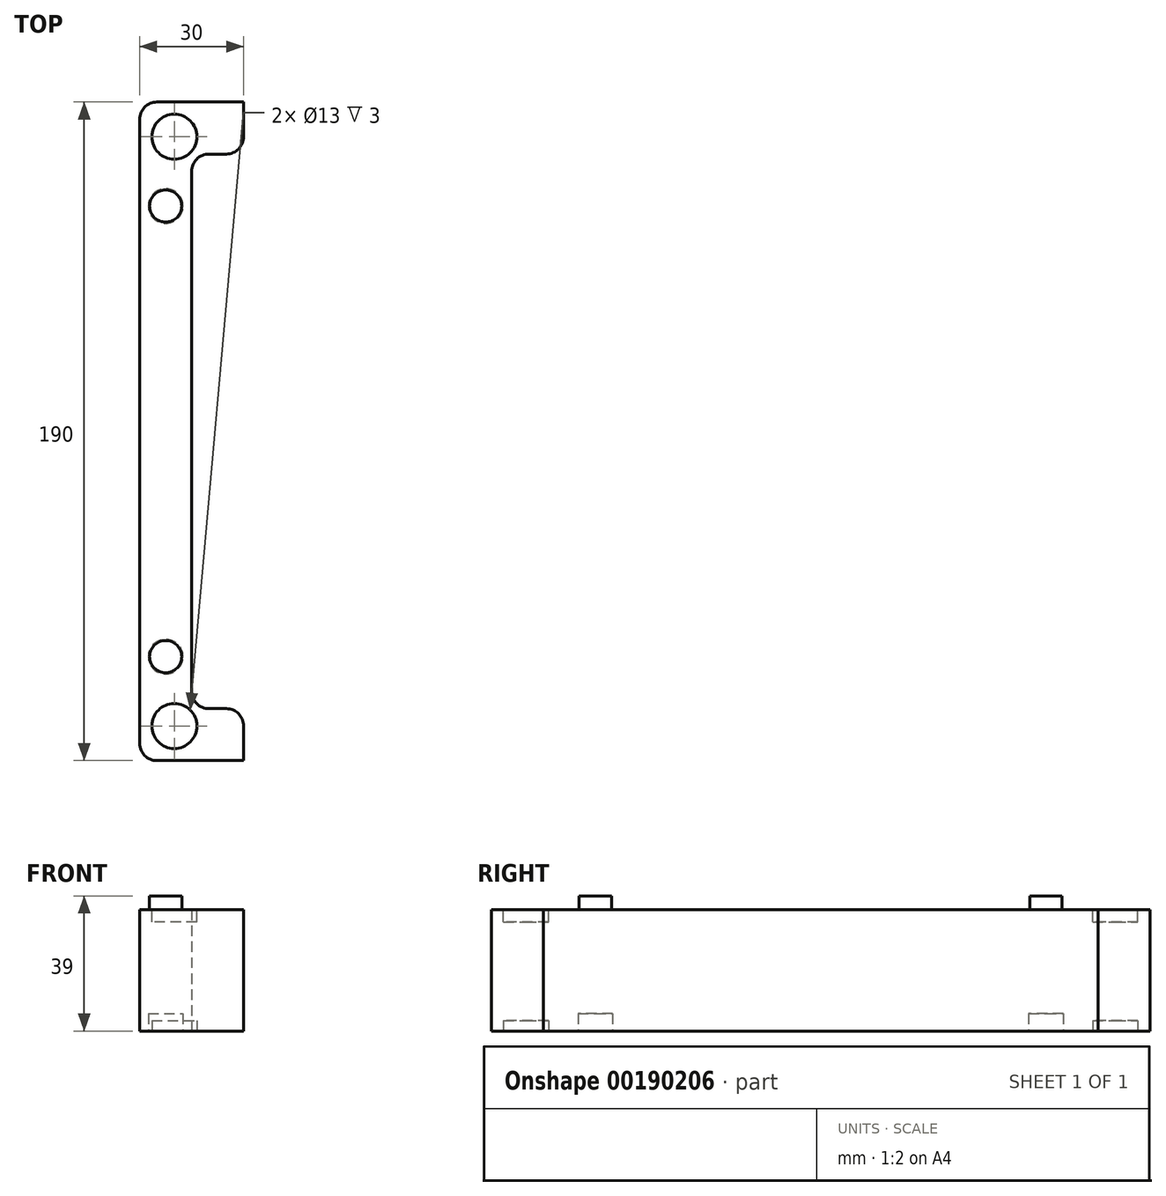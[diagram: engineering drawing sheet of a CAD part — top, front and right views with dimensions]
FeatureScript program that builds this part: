
annotation { "Feature Type Name" : "Feature", "Feature Type Description" : "" }
export const myFeature = defineFeature(function(context is Context, id is Id, definition is map)
    precondition{}
    {
        {
            var Q0;
            Q0=qCreatedBy(makeId("Top.planeOp"),FACE);
            var sketch = newSketch(context, id + "F0", { "sketchPlane" : qUnion([Q0])});
            skLineSegment(sketch, "E0.left", {"start": v(18.75, 91.13) * mm, "end": v(18.75, 81.13) * mm});
            skLineSegment(sketch, "E1", {"start": v(3.75, 71.13) * mm, "end": v(3.75, -78.87) * mm});
            skLineSegment(sketch, "E2", {"start": v(8.75, -83.87) * mm, "end": v(13.75, -83.87) * mm});
            skLineSegment(sketch, "E3", {"start": v(8.75, 76.13) * mm, "end": v(13.75, 76.13) * mm});
            skLineSegment(sketch, "E4.trimOffspring", {"start": v(18.75, -88.87) * mm, "end": v(18.75, -98.87) * mm});
            skLineSegment(sketch, "E5", {"start": v(18.75, 91.13) * mm, "end": v(-6.25, 91.13) * mm});
            skLineSegment(sketch, "E6", {"start": v(18.75, -98.87) * mm, "end": v(-6.25, -98.87) * mm});
            skLineSegment(sketch, "E7", {"start": v(-11.25, 86.13) * mm, "end": v(-11.25, -93.87) * mm});
            skPoint(sketch, "E8.visualSharp", {"position": v(-11.25, -98.87) * mm});
            skArc(sketch, "E8.filletArc", {"start": v(-11.25, -93.87) * mm, "mid": v(-9.79, -97.4) * mm, "end": v(-6.25, -98.87) * mm});
            skPoint(sketch, "E9.visualSharp", {"position": v(-11.25, 91.13) * mm});
            skArc(sketch, "E9.filletArc", {"start": v(-6.25, 91.13) * mm, "mid": v(-9.79, 89.66) * mm, "end": v(-11.25, 86.13) * mm});
            skPoint(sketch, "E10.visualSharp", {"position": v(18.75, 76.13) * mm});
            skArc(sketch, "E10.filletArc", {"start": v(13.75, 76.13) * mm, "mid": v(17.28, 77.6) * mm, "end": v(18.75, 81.13) * mm});
            skPoint(sketch, "E11.visualSharp", {"position": v(18.75, -83.87) * mm});
            skArc(sketch, "E11.filletArc", {"start": v(18.75, -88.87) * mm, "mid": v(17.28, -85.34) * mm, "end": v(13.75, -83.87) * mm});
            skPoint(sketch, "E12.visualSharp", {"position": v(3.75, -83.87) * mm});
            skArc(sketch, "E12.filletArc", {"start": v(3.75, -78.87) * mm, "mid": v(5.21, -82.4) * mm, "end": v(8.75, -83.87) * mm});
            skPoint(sketch, "E13.visualSharp", {"position": v(3.75, 76.13) * mm});
            skArc(sketch, "E13.filletArc", {"start": v(8.75, 76.13) * mm, "mid": v(5.21, 74.66) * mm, "end": v(3.75, 71.13) * mm});
            skSolve(sketch);
        }
        {
            var Q0;
            Q0 = qSketchRegion(id + "F0", true);
            extrude(context, id + "F1", {"entities" : qUnion([Q0]), "depth" : 35 * mm, "offsetDistance" : 25 * mm});
        }
        {
            var Q0;
            Q0=makeQuery(id+"F1.opExtrude","CAP_FACE",FACE,{"disambiguationData":[OSD([sQuery(id+"F0.wireOp",EDGE,"E0.left"),sQuery(id+"F0.wireOp",EDGE,"E1"),sQuery(id+"F0.wireOp",EDGE,"E2"),sQuery(id+"F0.wireOp",EDGE,"E3"),sQuery(id+"F0.wireOp",EDGE,"E4.trimOffspring"),sQuery(id+"F0.wireOp",EDGE,"E5"),sQuery(id+"F0.wireOp",EDGE,"E6"),sQuery(id+"F0.wireOp",EDGE,"E7"),sQuery(id+"F0.wireOp",EDGE,"E8.filletArc"),sQuery(id+"F0.wireOp",EDGE,"E9.filletArc"),sQuery(id+"F0.wireOp",EDGE,"E10.filletArc"),sQuery(id+"F0.wireOp",EDGE,"E11.filletArc"),sQuery(id+"F0.wireOp",EDGE,"E12.filletArc"),sQuery(id+"F0.wireOp",EDGE,"E13.filletArc")])],"isStart":false});
            var sketch = newSketch(context, id + "F2", { "sketchPlane" : qUnion([Q0])});
            skCircle(sketch, "E14", {"center": v(-1.25, 81.13) * mm, "radius": 6.5 * mm});
            skCircle(sketch, "E15", {"center": v(-1.25, -88.87) * mm, "radius": 6.5 * mm});
            skCircle(sketch, "E16", {"center": v(-3.75, 61.13) * mm, "radius": 4.65 * mm});
            skCircle(sketch, "E17", {"center": v(-3.75, -68.87) * mm, "radius": 4.65 * mm});
            skSolve(sketch);
        }
        {
            var Q0;
            Q0=makeQuery(id+"F1.opExtrude","CAP_FACE",FACE,{"disambiguationData":[OSD([sQuery(id+"F0.wireOp",EDGE,"E0.left"),sQuery(id+"F0.wireOp",EDGE,"E1"),sQuery(id+"F0.wireOp",EDGE,"E2"),sQuery(id+"F0.wireOp",EDGE,"E3"),sQuery(id+"F0.wireOp",EDGE,"E4.trimOffspring"),sQuery(id+"F0.wireOp",EDGE,"E5"),sQuery(id+"F0.wireOp",EDGE,"E6"),sQuery(id+"F0.wireOp",EDGE,"E7"),sQuery(id+"F0.wireOp",EDGE,"E8.filletArc"),sQuery(id+"F0.wireOp",EDGE,"E9.filletArc"),sQuery(id+"F0.wireOp",EDGE,"E10.filletArc"),sQuery(id+"F0.wireOp",EDGE,"E11.filletArc"),sQuery(id+"F0.wireOp",EDGE,"E12.filletArc"),sQuery(id+"F0.wireOp",EDGE,"E13.filletArc")])],"isStart":true});
            var sketch = newSketch(context, id + "F3", { "sketchPlane" : qUnion([Q0])});
            skCircle(sketch, "E18", {"center": v(-1.25, 88.87) * mm, "radius": 6.5 * mm});
            skCircle(sketch, "E19", {"center": v(-1.25, -81.13) * mm, "radius": 6.5 * mm});
            skCircle(sketch, "E20", {"center": v(-3.75, 68.87) * mm, "radius": 5 * mm});
            skCircle(sketch, "E21", {"center": v(-3.75, -61.13) * mm, "radius": 5 * mm});
            skSolve(sketch);
        }
        {
            var Q0;
            Q0=makeQuery(id+"F2.imprint","IMPRINT",FACE,{"disambiguationData":[TD([[makeQuery(id+"F2.imprint","IMPRINT",EDGE,{"derivedFrom":sQuery(id+"F2.wireOp",EDGE,"E14")}),1.0]])]});
            var Q1;
            Q1=makeQuery(id+"F2.imprint","IMPRINT",FACE,{"disambiguationData":[TD([[makeQuery(id+"F2.imprint","IMPRINT",EDGE,{"derivedFrom":sQuery(id+"F2.wireOp",EDGE,"E15")}),1.0]])]});
            extrude(context, id + "F4", {"entities" : qUnion([Q0, Q1]), "operationType" : NewBodyOperationType.REMOVE, "oppositeDirection" : true, "depth" : 3.5 * mm, "offsetDistance" : 25 * mm});
        }
        {
            var Q0;
            Q0=makeQuery(id+"F2.imprint","IMPRINT",FACE,{"disambiguationData":[TD([[makeQuery(id+"F2.imprint","IMPRINT",EDGE,{"derivedFrom":sQuery(id+"F2.wireOp",EDGE,"E16")}),1.0]])]});
            var Q1;
            Q1=makeQuery(id+"F2.imprint","IMPRINT",FACE,{"disambiguationData":[TD([[makeQuery(id+"F2.imprint","IMPRINT",EDGE,{"derivedFrom":sQuery(id+"F2.wireOp",EDGE,"E17")}),1.0]])]});
            extrude(context, id + "F5", {"entities" : qUnion([Q0, Q1]), "operationType" : NewBodyOperationType.ADD, "depth" : 4 * mm, "offsetDistance" : 25 * mm});
        }
        {
            var Q0;
            Q0=makeQuery(id+"F3.imprint","IMPRINT",FACE,{"disambiguationData":[TD([[makeQuery(id+"F3.imprint","IMPRINT",EDGE,{"derivedFrom":sQuery(id+"F3.wireOp",EDGE,"E19")}),1.0]])]});
            var Q1;
            Q1=makeQuery(id+"F3.imprint","IMPRINT",FACE,{"disambiguationData":[TD([[makeQuery(id+"F3.imprint","IMPRINT",EDGE,{"derivedFrom":sQuery(id+"F3.wireOp",EDGE,"E18")}),1.0]])]});
            extrude(context, id + "F6", {"entities" : qUnion([Q0, Q1]), "operationType" : NewBodyOperationType.REMOVE, "oppositeDirection" : true, "depth" : 3 * mm, "offsetDistance" : 25 * mm});
        }
        {
            var Q0;
            Q0=makeQuery(id+"F3.imprint","IMPRINT",FACE,{"disambiguationData":[TD([[makeQuery(id+"F3.imprint","IMPRINT",EDGE,{"derivedFrom":sQuery(id+"F3.wireOp",EDGE,"E21")}),1.0]])]});
            var Q1;
            Q1=makeQuery(id+"F3.imprint","IMPRINT",FACE,{"disambiguationData":[TD([[makeQuery(id+"F3.imprint","IMPRINT",EDGE,{"derivedFrom":sQuery(id+"F3.wireOp",EDGE,"E20")}),1.0]])]});
            extrude(context, id + "F7", {"entities" : qUnion([Q0, Q1]), "operationType" : NewBodyOperationType.REMOVE, "oppositeDirection" : true, "depth" : 5 * mm, "offsetDistance" : 25 * mm});
        }
    });
